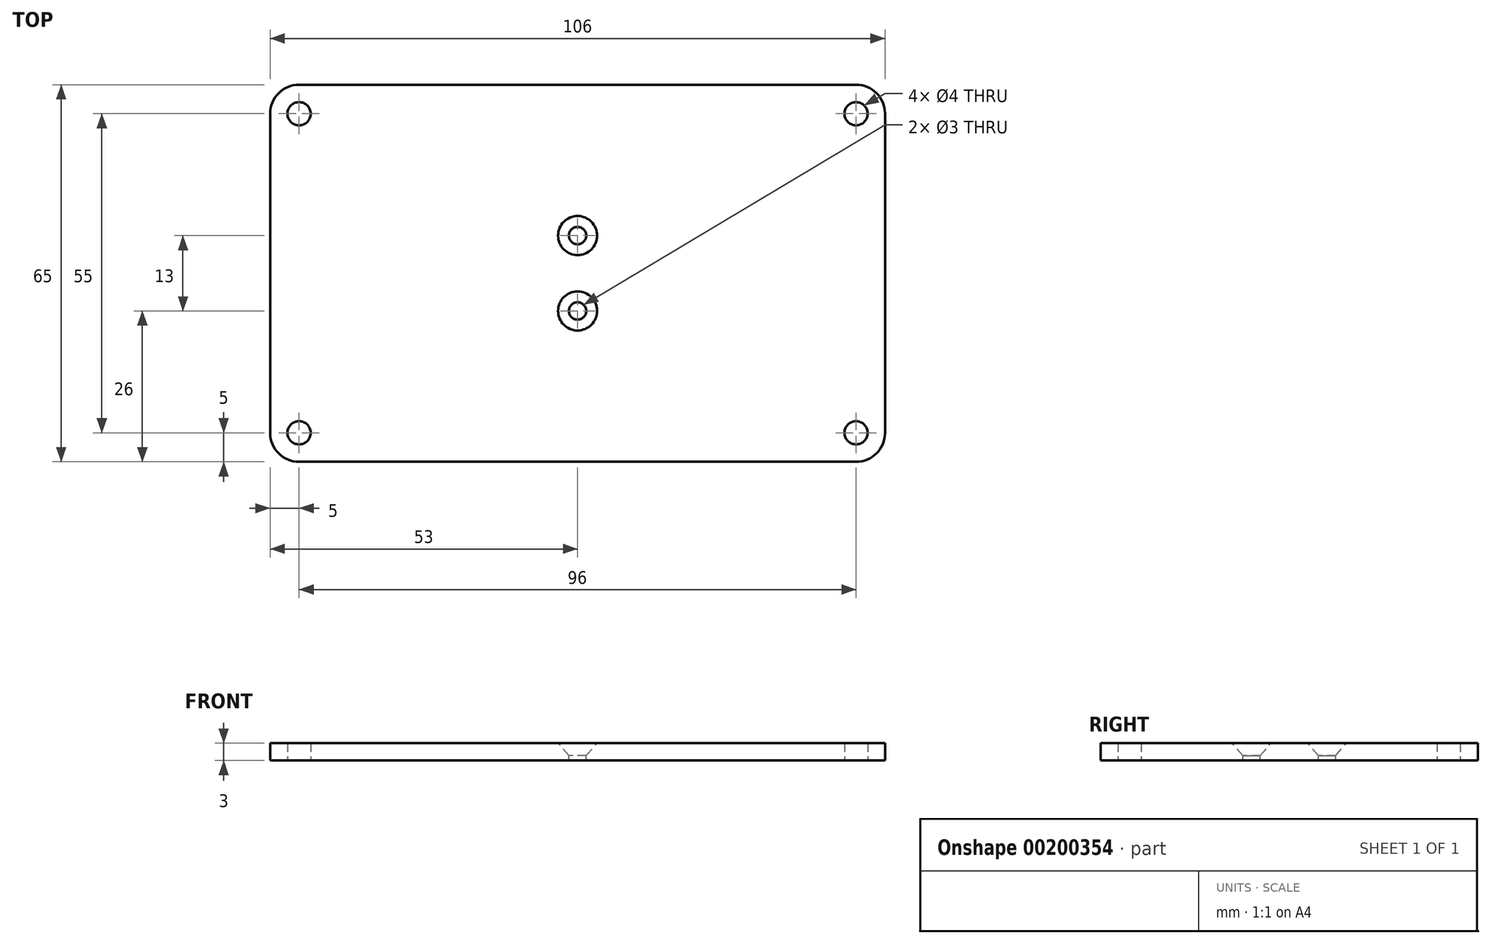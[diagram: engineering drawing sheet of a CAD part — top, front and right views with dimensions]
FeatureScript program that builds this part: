
annotation { "Feature Type Name" : "Feature", "Feature Type Description" : "" }
export const myFeature = defineFeature(function(context is Context, id is Id, definition is map)
    precondition{}
    {
        {
            var Q0;
            Q0=qCreatedBy(makeId("Top.planeOp"),FACE);
            var sketch = newSketch(context, id + "F0", { "sketchPlane" : qUnion([Q0])});
            skLineSegment(sketch, "E0.bottom", {"start": v(0, 0) * mm, "end": v(106, 0) * mm});
            skLineSegment(sketch, "E0.top", {"start": v(0, 65) * mm, "end": v(106, 65) * mm});
            skLineSegment(sketch, "E0.left", {"start": v(0, 0) * mm, "end": v(0, 65) * mm});
            skLineSegment(sketch, "E0.right", {"start": v(106, 0) * mm, "end": v(106, 65) * mm});
            skCircle(sketch, "E1", {"center": v(5, 60) * mm, "radius": 2 * mm});
            skCircle(sketch, "E2", {"center": v(101, 60) * mm, "radius": 2 * mm});
            skCircle(sketch, "E3", {"center": v(5, 5) * mm, "radius": 2 * mm});
            skCircle(sketch, "E4", {"center": v(101, 5) * mm, "radius": 2 * mm});
            skLineSegment(sketch, "E5", {"start": v(5, 60) * mm, "end": v(5, 5) * mm, "construction": true});
            skLineSegment(sketch, "E6", {"start": v(5, 5) * mm, "end": v(101, 5) * mm, "construction": true});
            skLineSegment(sketch, "E7", {"start": v(101, 5) * mm, "end": v(101, 60) * mm, "construction": true});
            skLineSegment(sketch, "E8", {"start": v(101, 60) * mm, "end": v(5, 60) * mm, "construction": true});
            skLineSegment(sketch, "E9", {"start": v(5, 60) * mm, "end": v(0, 65) * mm, "construction": true});
            skLineSegment(sketch, "E10", {"start": v(5, 5) * mm, "end": v(0, 0) * mm, "construction": true});
            skLineSegment(sketch, "E11", {"start": v(101, 60) * mm, "end": v(106, 65) * mm, "construction": true});
            skSolve(sketch);
        }
        {
            var Q0;
            Q0=makeQuery(id+"F0.imprint","IMPRINT",FACE,{"disambiguationData":[TD([[makeQuery(id+"F0.imprint","IMPRINT",EDGE,{"derivedFrom":sQuery(id+"F0.wireOp",EDGE,"E0.bottom")}),1.0]])]});
            extrude(context, id + "F1", {"entities" : qUnion([Q0]), "depth" : 3 * mm});
        }
        {
            var Q0;
            Q0=makeQuery(id+"F1.opExtrude","CAP_FACE",FACE,{"disambiguationData":[OSD([sQuery(id+"F0.wireOp",EDGE,"E0.bottom"),sQuery(id+"F0.wireOp",EDGE,"E0.top"),sQuery(id+"F0.wireOp",EDGE,"E0.left"),sQuery(id+"F0.wireOp",EDGE,"E0.right"),sQuery(id+"F0.wireOp",EDGE,"E1"),sQuery(id+"F0.wireOp",EDGE,"E2"),sQuery(id+"F0.wireOp",EDGE,"E3"),sQuery(id+"F0.wireOp",EDGE,"E4")])],"isStart":false});
            var sketch = newSketch(context, id + "F2", { "sketchPlane" : qUnion([Q0])});
            skPoint(sketch, "E12", {"position": v(53, 39) * mm});
            skPoint(sketch, "E13", {"position": v(53, 26) * mm});
            skLineSegment(sketch, "E14", {"start": v(53, 39) * mm, "end": v(53, 26) * mm, "construction": true});
            skLineSegment(sketch, "E15", {"start": v(53, 39) * mm, "end": v(53, 65) * mm, "construction": true});
            skSolve(sketch);
        }
        {
            var Q0;
            Q0=sQuery(id+"F2.wireOp",VERTEX,"E12");
            var Q1;
            Q1=sQuery(id+"F2.wireOp",VERTEX,"E13");
            var Q2;
            Q2=makeQuery(id+"F1.opExtrude","SWEPT_BODY",BODY,{"disambiguationData":[OSD([sQuery(id+"F0.wireOp",EDGE,"E0.bottom"),sQuery(id+"F0.wireOp",EDGE,"E0.top"),sQuery(id+"F0.wireOp",EDGE,"E0.left"),sQuery(id+"F0.wireOp",EDGE,"E0.right"),sQuery(id+"F0.wireOp",EDGE,"E1"),sQuery(id+"F0.wireOp",EDGE,"E2"),sQuery(id+"F0.wireOp",EDGE,"E3"),sQuery(id+"F0.wireOp",EDGE,"E4")])]});
            hole(context, id + "F3", {"style" : HoleStyle.C_SINK, "endStyle" : HoleEndStyle.THROUGH, "holeDiameter" : 3 * mm, "cSinkDiameter" : 6.72 * mm, "cSinkAngle" : 82 * degree, "locations" : qUnion([Q0, Q1]), "scope" : qUnion([Q2]), "isTappedThrough" : true});
        }
        {
            var Q0;
            Q0=makeQuery(id+"F1.opExtrude","SWEPT_EDGE",EDGE,{"disambiguationData":[OSD([sQuery(id+"F0.wireOp",EDGE,"E0.bottom"),sQuery(id+"F0.wireOp",EDGE,"E0.right")])]});
            var Q1;
            Q1=makeQuery(id+"F1.opExtrude","SWEPT_EDGE",EDGE,{"disambiguationData":[OSD([sQuery(id+"F0.wireOp",EDGE,"E0.bottom"),sQuery(id+"F0.wireOp",EDGE,"E0.left")])]});
            var Q2;
            Q2=makeQuery(id+"F1.opExtrude","SWEPT_EDGE",EDGE,{"disambiguationData":[OSD([sQuery(id+"F0.wireOp",EDGE,"E0.top"),sQuery(id+"F0.wireOp",EDGE,"E0.left")])]});
            var Q3;
            Q3=makeQuery(id+"F1.opExtrude","SWEPT_EDGE",EDGE,{"disambiguationData":[OSD([sQuery(id+"F0.wireOp",EDGE,"E0.top"),sQuery(id+"F0.wireOp",EDGE,"E0.right")])]});
            fillet(context, id + "F4", {"entities" : qUnion([Q0, Q1, Q2, Q3]), "radius" : 5 * mm, "tangentPropagation" : true, "allowEdgeOverflow" : false});
        }
    });
